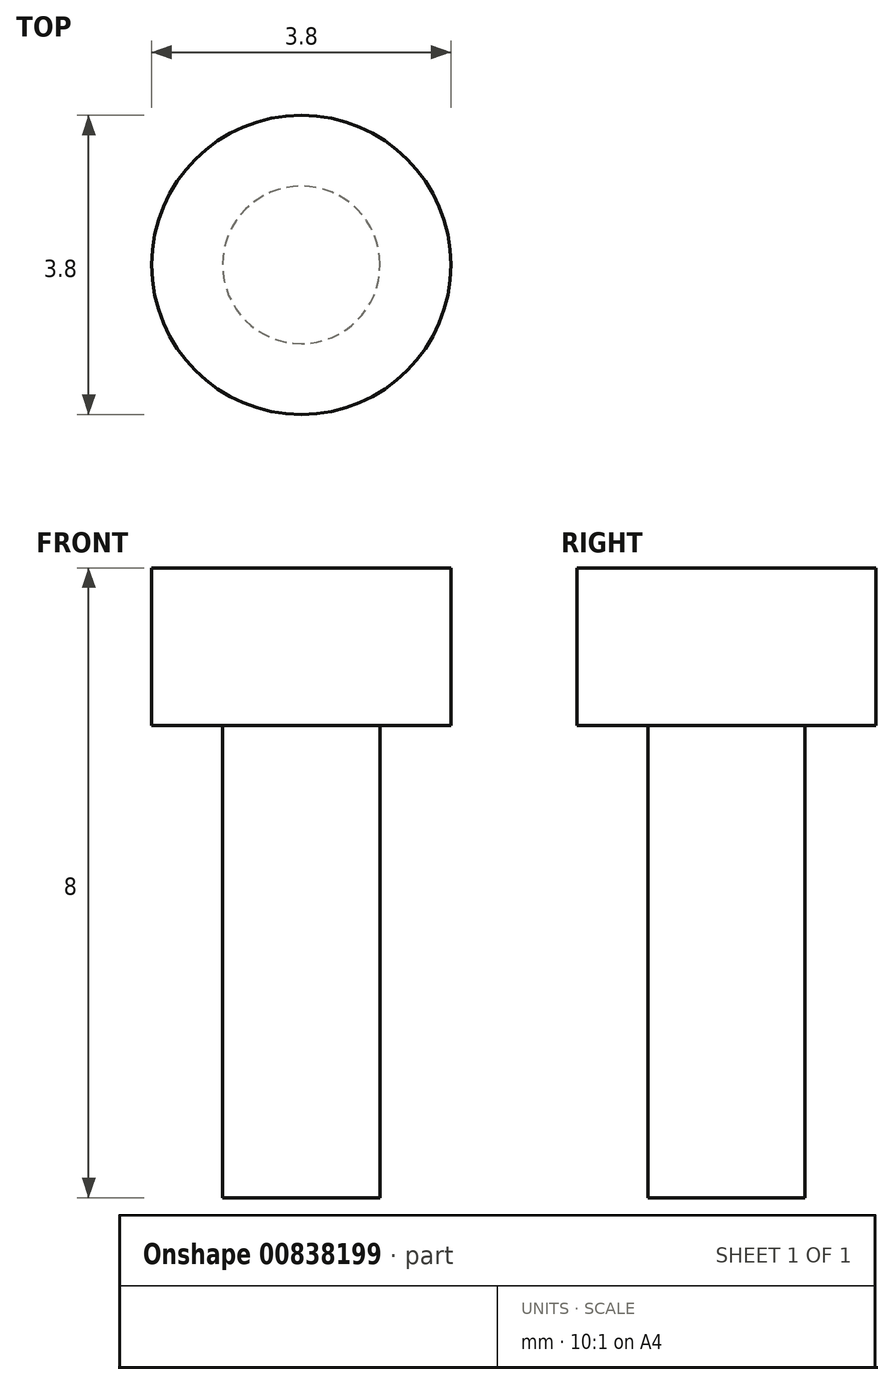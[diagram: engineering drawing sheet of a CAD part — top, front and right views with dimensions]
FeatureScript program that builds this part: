
annotation { "Feature Type Name" : "Feature", "Feature Type Description" : "" }
export const myFeature = defineFeature(function(context is Context, id is Id, definition is map)
    precondition{}
    {
        {
            var Q0;
            Q0=qCreatedBy(makeId("Right.planeOp"),FACE);
            var sketch = newSketch(context, id + "F0", { "sketchPlane" : qUnion([Q0])});
            skLineSegment(sketch, "E0", {"start": v(0, -4.8) * mm, "end": v(1, -4.8) * mm});
            skLineSegment(sketch, "E1", {"start": v(1, -4.8) * mm, "end": v(1, 1.2) * mm});
            skLineSegment(sketch, "E2", {"start": v(1, 1.2) * mm, "end": v(1.9, 1.2) * mm});
            skLineSegment(sketch, "E3", {"start": v(1.9, 1.2) * mm, "end": v(1.9, 3.2) * mm});
            skLineSegment(sketch, "E4", {"start": v(1.9, 3.2) * mm, "end": v(0, 3.2) * mm});
            skLineSegment(sketch, "E5.MirrorCS", {"start": v(0, -4.8) * mm, "end": v(-1, -4.8) * mm});
            skLineSegment(sketch, "E6.MirrorCS", {"start": v(-1, -4.8) * mm, "end": v(-1, 1.2) * mm});
            skLineSegment(sketch, "E7.MirrorCS", {"start": v(-1, 1.2) * mm, "end": v(-1.9, 1.2) * mm});
            skLineSegment(sketch, "E8.MirrorCS", {"start": v(-1.9, 1.2) * mm, "end": v(-1.9, 3.2) * mm});
            skLineSegment(sketch, "E9.MirrorCS", {"start": v(-1.9, 3.2) * mm, "end": v(0, 3.2) * mm});
            skLineSegment(sketch, "E10", {"start": v(0, -4.8) * mm, "end": v(0, 3.2) * mm});
            skSolve(sketch);
        }
        {
            var Q0;
            Q0=makeQuery(id+"F0.imprint","IMPRINT",FACE,{"disambiguationData":[TD([[makeQuery(id+"F0.imprint","IMPRINT",EDGE,{"derivedFrom":sQuery(id+"F0.wireOp",EDGE,"E5.MirrorCS")}),-1.0]])]});
            var Q1;
            Q1=sQuery(id+"F0.wireOp",EDGE,"E10");
            revolve(context, id + "F1", {"surfaceOperationType" : NewSurfaceOperationType.NEW, "entities" : qUnion([Q0]), "axis" : qUnion([Q1]), "revolveType" : RevolveType.FULL});
        }
    });
